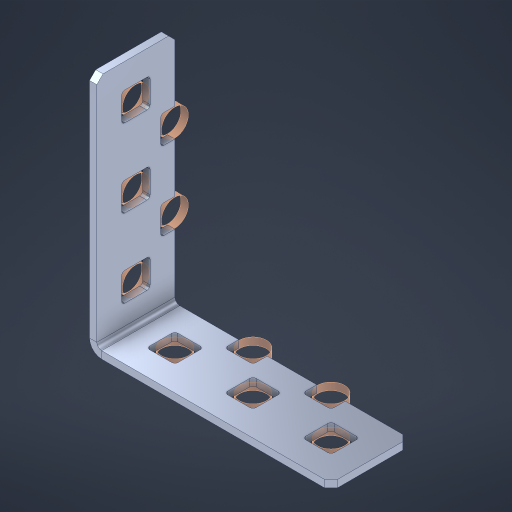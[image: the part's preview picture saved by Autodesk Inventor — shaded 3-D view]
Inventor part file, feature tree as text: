
AUTODESK INVENTOR PART (.ipt)
format: ipt  version: 2023 (Build 270158000, 158)  size: 537,600 bytes
history: native  units: in
note: dims shown in document units (in); Inventor stores cm internally (conversion verified against a paired STEP export)
features: other x148, extrude x140, sheet_metal_op x8, sketch x7, pattern_linear x3, mirror x1, chamfer x1
ambient origin geometry x8: Origin, YZ Plane, XZ Plane, XY Plane, X Axis, Y Axis, Z Axis, Center Point
bodies: Solid1 (feature_tree), Body (feature_tree)
feature tree (308):
  sheet_metal_op  "Flanges"
  sheet_metal_op  "Body Pattern"
  pattern_linear  "Center Double"  Spacing1=1.5in  [1 undecoded]
  pattern_linear  "Center Pattern"  Spacing1=0.1875in  [1 undecoded]
  other  "Arc Length"
  pattern_linear  "Notch Pattern"  Spacing1=0.0469in  [1 undecoded]
  other  "Diagonal Plane"
  mirror  "Everything Mirrored"
  chamfer  "End Chamfer"
  sketch  "Sketch1"  dims[d0=1.5in]
  other  "Plate1"
  sketch  "Sketch2"  dims[d1=0.5in]
  other  "Plate2"
  sheet_metal_op  "Bend1"
  sheet_metal_op  "Corner1"
  sketch  "Sketch8"  dims[d2=0.0469in]
  sketch  "Sketch9"  dims[d3=0.0469in]
  other  "Srf91"
  sheet_metal_op  "Body Pattern Sketch"
  other  "Srf92"
  sketch  "Sketch13"  dims[d4=0.0234in]
  sketch  "Sketch15"  dims[d5=0.0938in]
  sketch  "Sketch16"  dims[d6=0.0469in d7=1.5in d8=90.0deg d9=0.0312in d10=0.1875in d11=0.0469in d12=0.0469in d49=0.182in d50=0.02in d52=0.25in d53=0.0469in d54=0.0in d55=0.172in d56=1.0in d57=0.0in d85=0.1473in d86=0.1659in d89=0.0469in d90=0.0in d91=0.04in d92=0.0491in d95=2.5in d96=0.04in d97=0.25in d98=45.0deg d106=0.182in d107=0.02in d110=0.0469in d111=0.0in d112=0.172in d113=0.5in d114=0.0in d117=0.5in d126=0.0491in d127=0.1227in d128=0.08in d129=0.04in d130=2.5in d131=0.25in d132=0.3937in d134=0.5in d135=1.1811in d137=0.5in d140=0.5in d141=1.0in d142=0.3937in d144=0.5in d145=0.071in d146=0.7874in d148=0.5in]
  other  "Srf786"
  other  "Srf856"
  other  "Srf889"
  other  "Srf890"
  other  "Srf891"
  other  "Srf1275"
  other  "Srf1276"
  other  "Srf1278"
  other  "Srf1277"
  other  "Srf1285"
  other  "Srf1286"
  other  "Srf1287"
  other  "Srf1445"
  other  "Srf1446"
  other  "Srf1447"
  other  "Srf1448"
  other  "Srf1449"
  other  "Srf1537"
  other  "Srf1538"
  other  "Srf1539"
  other  "Srf1540"
  other  "Srf1541"
  other  "Srf1807"
  other  "Srf1808"
  other  "Srf1809"
  other  "Srf1810"
  other  "Srf1811"
  other  "Srf1812"
  other  "Srf1813"
  other  "Srf1814"
  other  "Srf1815"
  other  "Srf1816"
  other  "Srf1817"
  other  "Srf1818"
  other  "Srf1819"
  other  "Srf1820"
  other  "Srf1821"
  other  "Srf1822"
  other  "Srf1823"
  other  "Srf1824"
  other  "Srf1825"
  other  "Srf1826"
  other  "Srf1827"
  other  "Srf1828"
  other  "Srf1829"
  other  "Srf1830"
  other  "Srf1831"
  other  "Srf1959"
  other  "Srf1960"
  other  "Srf1961"
  other  "Srf1962"
  other  "Srf1963"
  other  "Srf1964"
  other  "Srf1965"
  other  "Srf1966"
  other  "Srf1967"
  other  "Srf1968"
  other  "Srf1969"
  other  "Srf1970"
  other  "Srf1971"
  other  "Srf1972"
  other  "Srf1973"
  other  "Srf1974"
  other  "Srf1975"
  other  "Srf1976"
  other  "Srf1977"
  other  "Srf1978"
  other  "Srf1979"
  other  "Srf1980"
  other  "Srf1981"
  other  "Srf1982"
  other  "Srf1983"
  other  "Srf2009"
  other  "Srf2010"
  other  "Srf2011"
  other  "Srf2012"
  other  "Srf2013"
  other  "Srf2014"
  other  "Srf2015"
  other  "Srf2016"
  other  "Srf2017"
  other  "Srf2018"
  other  "Srf2019"
  other  "Srf2020"
  other  "Srf2021"
  other  "Srf2022"
  other  "Srf2023"
  other  "Srf2024"
  other  "Srf2025"
  other  "Srf2026"
  other  "Srf2027"
  other  "Srf2028"
  other  "Srf2029"
  other  "Srf2030"
  other  "Srf2031"
  other  "Srf2032"
  other  "Srf2033"
  other  "Srf2034"
  other  "Srf2035"
  other  "Srf2036"
  other  "Srf2037"
  other  "Srf2038"
  other  "Srf2039"
  other  "Srf2040"
  other  "Srf2041"
  other  "Srf2042"
  other  "Srf2043"
  other  "Srf2044"
  other  "Srf2045"
  other  "Srf2046"
  other  "Srf2047"
  other  "Srf2048"
  other  "Srf2049"
  other  "Srf2050"
  other  "Srf2051"
  other  "Srf2052"
  other  "Srf2053"
  other  "Srf2054"
  other  "Srf2055"
  other  "Srf2056"
  other  "Srf2057"
  other  "Srf2058"
  other  "Srf2059"
  other  "Srf2060"
  other  "Srf2061"
  other  "Srf2062"
  other  "Srf2063"
  other  "Srf2064"
  other  "Srf2065"
  other  "Srf2066"
  other  "Srf2067"
  other  "Srf2068"
  other  "Srf2069"
  other  "Srf2070"
  other  "Srf2071"
  other  "Srf2072"
  other  "Srf2073"
  other  "Srf2074"
  other  "Srf2075"
  other  "Srf2076"
  sheet_metal_op  "Body Stamp"
  sheet_metal_op  "Body Circle"
  other  "Center Stamp"
  other  "Center Circle"
  sheet_metal_op  "Notch"
  extrude  "ExtrusionSrf92"  Depth=0.0469in
  extrude  "ExtrusionSrf856"  Depth=0.182in
  extrude  "ExtrusionSrf889"  Depth=0.02in
  extrude  "ExtrusionSrf890"  Depth=0.25in
  extrude  "ExtrusionSrf891"  Depth=0.0469in
  extrude  "ExtrusionSrf1275"  TaperAngle=0.0deg  [1 undecoded]
  extrude  "ExtrusionSrf1276"  Depth=0.5in
  extrude  "ExtrusionSrf1277"  Depth=1.0in TaperAngle=0.0deg
  extrude  "ExtrusionSrf1345"  Depth=0.5in
  extrude  "ExtrusionSrf1346"  Depth=0.5in
  extrude  "ExtrusionSrf1347"  Depth=0.0469in
  extrude  "ExtrusionSrf1348"  Depth=0.5in TaperAngle=0.0deg
  extrude  "ExtrusionSrf1445"  Depth=0.5in
  extrude  "ExtrusionSrf1446"  Depth=0.25in TaperAngle=45.0deg
  extrude  "ExtrusionSrf1447"  Depth=0.182in
  extrude  "ExtrusionSrf1448"  Depth=0.02in
  extrude  "ExtrusionSrf1449"  Depth=0.0469in
  extrude  "ExtrusionSrf1537"  TaperAngle=0.0deg  [1 undecoded]
  extrude  "ExtrusionSrf1538"  Depth=0.5in
  extrude  "ExtrusionSrf1539"  Depth=0.5in TaperAngle=0.0deg
  extrude  "ExtrusionSrf1540"  Depth=0.5in
  extrude  "ExtrusionSrf1541"  Depth=0.5in
  extrude  "ExtrusionSrf1807"  Depth=0.5in
  extrude  "ExtrusionSrf1808"  Depth=0.5in
  extrude  "ExtrusionSrf1809"  Depth=0.5in
  extrude  "ExtrusionSrf1810"  Depth=0.5in
  extrude  "ExtrusionSrf1811"  Depth=0.25in
  extrude  "ExtrusionSrf1812"  Depth=0.3937in
  extrude  "ExtrusionSrf1813"  Depth=0.5in
  extrude  "ExtrusionSrf1814"  Depth=0.5in
  extrude  "ExtrusionSrf1815"  Depth=1.0in
  extrude  "ExtrusionSrf1816"  Depth=0.3937in
  extrude  "ExtrusionSrf1817"  Depth=0.5in
  extrude  "ExtrusionSrf1818"  Depth=0.5in
  extrude  "ExtrusionSrf1819"  [1 undecoded]
  extrude  "ExtrusionSrf1820"  [1 undecoded]
  extrude  "ExtrusionSrf1821"  [1 undecoded]
  extrude  "ExtrusionSrf1822"  [1 undecoded]
  extrude  "ExtrusionSrf1823"  [1 undecoded]
  extrude  "ExtrusionSrf1824"  [1 undecoded]
  extrude  "ExtrusionSrf1825"  [1 undecoded]
  extrude  "ExtrusionSrf1826"  [1 undecoded]
  extrude  "ExtrusionSrf1827"  [1 undecoded]
  extrude  "ExtrusionSrf1828"  [1 undecoded]
  extrude  "ExtrusionSrf1829"  [1 undecoded]
  extrude  "ExtrusionSrf1830"  [1 undecoded]
  extrude  "ExtrusionSrf1831"  [1 undecoded]
  extrude  "ExtrusionSrf1959"  [1 undecoded]
  extrude  "ExtrusionSrf1960"  [1 undecoded]
  extrude  "ExtrusionSrf1961"  [1 undecoded]
  extrude  "ExtrusionSrf1962"  [1 undecoded]
  extrude  "ExtrusionSrf1963"  [1 undecoded]
  extrude  "ExtrusionSrf1964"  [1 undecoded]
  extrude  "ExtrusionSrf1965"  [1 undecoded]
  extrude  "ExtrusionSrf1966"  [1 undecoded]
  extrude  "ExtrusionSrf1967"  [1 undecoded]
  extrude  "ExtrusionSrf1968"  [1 undecoded]
  extrude  "ExtrusionSrf1969"  [1 undecoded]
  extrude  "ExtrusionSrf1970"  [1 undecoded]
  extrude  "ExtrusionSrf1971"  [1 undecoded]
  extrude  "ExtrusionSrf1972"  [1 undecoded]
  extrude  "ExtrusionSrf1973"  [1 undecoded]
  extrude  "ExtrusionSrf1974"  [1 undecoded]
  extrude  "ExtrusionSrf1975"  [1 undecoded]
  extrude  "ExtrusionSrf1976"  [1 undecoded]
  extrude  "ExtrusionSrf1977"  [1 undecoded]
  extrude  "ExtrusionSrf1978"  [1 undecoded]
  extrude  "ExtrusionSrf1979"  [1 undecoded]
  extrude  "ExtrusionSrf1980"  [1 undecoded]
  extrude  "ExtrusionSrf1981"  [1 undecoded]
  extrude  "ExtrusionSrf1982"  [1 undecoded]
  extrude  "ExtrusionSrf1983"  [1 undecoded]
  extrude  "ExtrusionSrf2009"  [1 undecoded]
  extrude  "ExtrusionSrf2010"  [1 undecoded]
  extrude  "ExtrusionSrf2011"  [1 undecoded]
  extrude  "ExtrusionSrf2012"  [1 undecoded]
  extrude  "ExtrusionSrf2013"  [1 undecoded]
  extrude  "ExtrusionSrf2014"  [1 undecoded]
  extrude  "ExtrusionSrf2015"  [1 undecoded]
  extrude  "ExtrusionSrf2016"  [1 undecoded]
  extrude  "ExtrusionSrf2017"  [1 undecoded]
  extrude  "ExtrusionSrf2018"  [1 undecoded]
  extrude  "ExtrusionSrf2019"  [1 undecoded]
  extrude  "ExtrusionSrf2020"  [1 undecoded]
  extrude  "ExtrusionSrf2021"  [1 undecoded]
  extrude  "ExtrusionSrf2022"  [1 undecoded]
  extrude  "ExtrusionSrf2023"  [1 undecoded]
  extrude  "ExtrusionSrf2024"  [1 undecoded]
  extrude  "ExtrusionSrf2025"  [1 undecoded]
  extrude  "ExtrusionSrf2026"  [1 undecoded]
  extrude  "ExtrusionSrf2027"  [1 undecoded]
  extrude  "ExtrusionSrf2028"  [1 undecoded]
  extrude  "ExtrusionSrf2029"  [1 undecoded]
  extrude  "ExtrusionSrf2030"  [1 undecoded]
  extrude  "ExtrusionSrf2031"  [1 undecoded]
  extrude  "ExtrusionSrf2032"  [1 undecoded]
  extrude  "ExtrusionSrf2033"  [1 undecoded]
  extrude  "ExtrusionSrf2034"  [1 undecoded]
  extrude  "ExtrusionSrf2035"  [1 undecoded]
  extrude  "ExtrusionSrf2036"  [1 undecoded]
  extrude  "ExtrusionSrf2037"  [1 undecoded]
  extrude  "ExtrusionSrf2038"  [1 undecoded]
  extrude  "ExtrusionSrf2039"  [1 undecoded]
  extrude  "ExtrusionSrf2040"  [1 undecoded]
  extrude  "ExtrusionSrf2041"  [1 undecoded]
  extrude  "ExtrusionSrf2042"  [1 undecoded]
  extrude  "ExtrusionSrf2043"  [1 undecoded]
  extrude  "ExtrusionSrf2044"  [1 undecoded]
  extrude  "ExtrusionSrf2045"  [1 undecoded]
  extrude  "ExtrusionSrf2046"  [1 undecoded]
  extrude  "ExtrusionSrf2047"  [1 undecoded]
  extrude  "ExtrusionSrf2048"  [1 undecoded]
  extrude  "ExtrusionSrf2049"  [1 undecoded]
  extrude  "ExtrusionSrf2050"  [1 undecoded]
  extrude  "ExtrusionSrf2051"  [1 undecoded]
  extrude  "ExtrusionSrf2052"  [1 undecoded]
  extrude  "ExtrusionSrf2053"  [1 undecoded]
  extrude  "ExtrusionSrf2054"  [1 undecoded]
  extrude  "ExtrusionSrf2055"  [1 undecoded]
  extrude  "ExtrusionSrf2056"  [1 undecoded]
  extrude  "ExtrusionSrf2057"  [1 undecoded]
  extrude  "ExtrusionSrf2058"  [1 undecoded]
  extrude  "ExtrusionSrf2059"  [1 undecoded]
  extrude  "ExtrusionSrf2060"  [1 undecoded]
  extrude  "ExtrusionSrf2061"  [1 undecoded]
  extrude  "ExtrusionSrf2062"  [1 undecoded]
  extrude  "ExtrusionSrf2063"  [1 undecoded]
  extrude  "ExtrusionSrf2064"  [1 undecoded]
  extrude  "ExtrusionSrf2065"  [1 undecoded]
  extrude  "ExtrusionSrf2066"  [1 undecoded]
  extrude  "ExtrusionSrf2067"  [1 undecoded]
  extrude  "ExtrusionSrf2068"  [1 undecoded]
  extrude  "ExtrusionSrf2069"  [1 undecoded]
  extrude  "ExtrusionSrf2070"  [1 undecoded]
  extrude  "ExtrusionSrf2071"  [1 undecoded]
  extrude  "ExtrusionSrf2072"  [1 undecoded]
  extrude  "ExtrusionSrf2073"  [1 undecoded]
  extrude  "ExtrusionSrf2074"  [1 undecoded]
  extrude  "ExtrusionSrf2075"  [1 undecoded]
  extrude  "ExtrusionSrf2076"  [1 undecoded]
note: 111 required parameter values undecoded (feature->parameter linkage not recoverable at this tier; creation-order binding heuristic only, values carry confidence <= 0.55)
